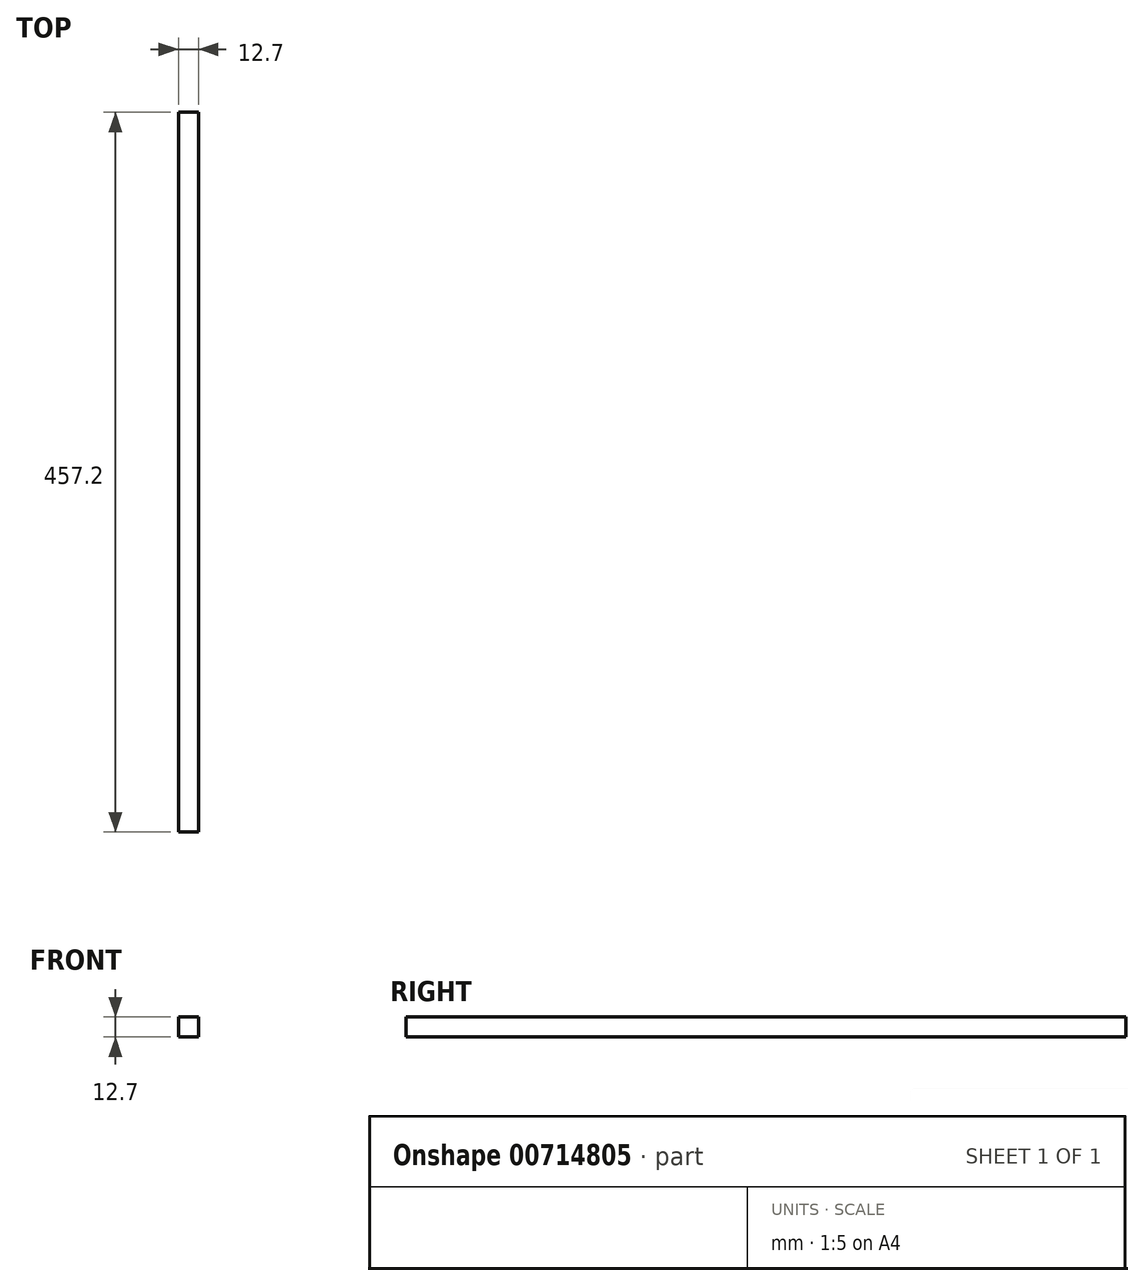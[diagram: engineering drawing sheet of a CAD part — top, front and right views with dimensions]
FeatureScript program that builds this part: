
annotation { "Feature Type Name" : "Feature", "Feature Type Description" : "" }
export const myFeature = defineFeature(function(context is Context, id is Id, definition is map)
    precondition{}
    {
        {
            var Q0;
            Q0=qCreatedBy(makeId("Right.planeOp"),FACE);
            var sketch = newSketch(context, id + "F0", { "sketchPlane" : qUnion([Q0])});
            skLineSegment(sketch, "E0.bottom", {"start": v(0, 0) * mm, "end": v(457.2, 0) * mm});
            skLineSegment(sketch, "E0.top", {"start": v(0, 12.7) * mm, "end": v(457.2, 12.7) * mm});
            skLineSegment(sketch, "E0.left", {"start": v(0, 0) * mm, "end": v(0, 12.7) * mm});
            skLineSegment(sketch, "E0.right", {"start": v(457.2, 0) * mm, "end": v(457.2, 12.7) * mm});
            skSolve(sketch);
        }
        {
            var Q0;
            Q0 = qSketchRegion(id + "F0", true);
            extrude(context, id + "F1", {"entities" : qUnion([Q0]), "depth" : 12.7 * mm, "offsetDistance" : 25.4 * mm});
        }
    });
